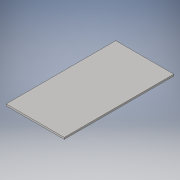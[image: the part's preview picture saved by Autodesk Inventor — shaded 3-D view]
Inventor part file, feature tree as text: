
AUTODESK INVENTOR PART (.ipt)
format: ipt  version: 2016 (Build 200138000, 138)  size: 83,968 bytes
history: native  units: in
note: dims shown in document units (in); Inventor stores cm internally (conversion verified against a paired STEP export)
features: extrude x1, sketch x1
ambient origin geometry x8: Origin, YZ Plane, XZ Plane, XY Plane, X Axis, Y Axis, Z Axis, Center Point
bodies: Solid1 (feature_tree)
feature tree (2):
  extrude  "Extrusion1"  [1 undecoded]
  sketch  "Sketch1"  dims[d0=0.1in d1=0.0in]
note: 1 required parameter value undecoded (feature->parameter linkage not recoverable at this tier; creation-order binding heuristic only, values carry confidence <= 0.55)
